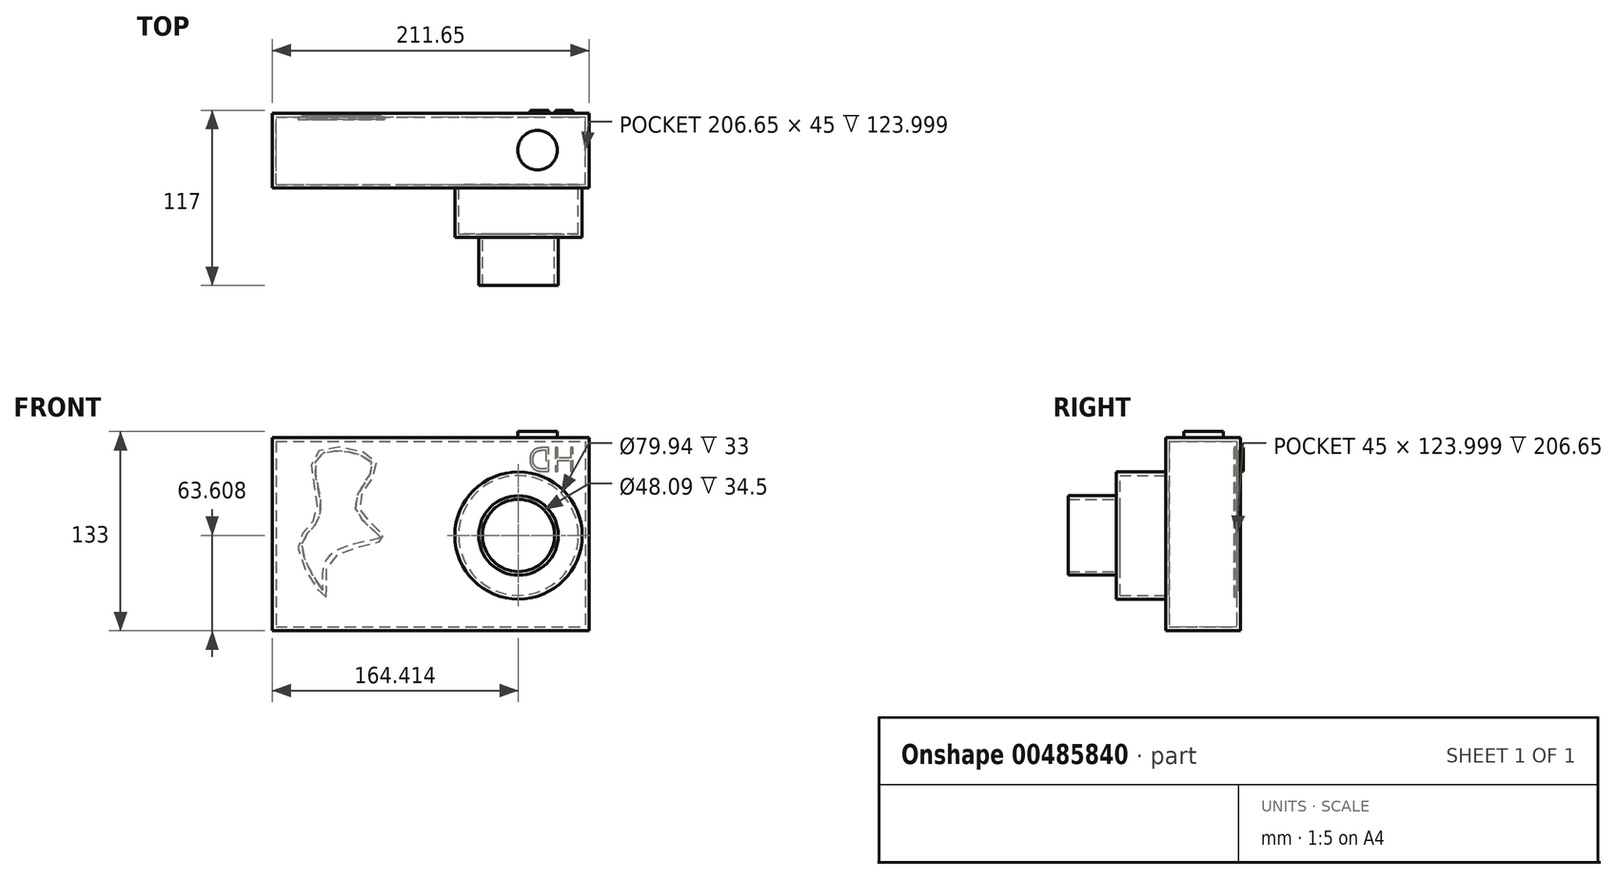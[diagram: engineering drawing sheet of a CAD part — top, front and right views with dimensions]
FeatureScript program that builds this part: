
annotation { "Feature Type Name" : "Feature", "Feature Type Description" : "" }
export const myFeature = defineFeature(function(context is Context, id is Id, definition is map)
    precondition{}
    {
        {
            var Q0;
            Q0=qCreatedBy(makeId("Front.planeOp"),FACE);
            var sketch = newSketch(context, id + "F0", { "sketchPlane" : qUnion([Q0])});
            skLineSegment(sketch, "E0.bottom", {"start": v(-118.11, 60.74) * mm, "end": v(93.54, 60.74) * mm});
            skLineSegment(sketch, "E0.top", {"start": v(-118.11, -68.26) * mm, "end": v(93.54, -68.26) * mm});
            skLineSegment(sketch, "E0.left", {"start": v(-118.11, 60.74) * mm, "end": v(-118.11, -68.26) * mm});
            skLineSegment(sketch, "E0.right", {"start": v(93.54, 60.74) * mm, "end": v(93.54, -68.26) * mm});
            skSolve(sketch);
        }
        {
            var Q0;
            Q0 = qSketchRegion(id + "F0", true);
            extrude(context, id + "F1", {"entities" : qUnion([Q0]), "depth" : 50 * mm});
        }
        {
            var Q0;
            Q0=makeQuery(id+"F1.opExtrude","CAP_FACE",FACE,{"disambiguationData":[OSD([sQuery(id+"F0.wireOp",EDGE,"E0.bottom"),sQuery(id+"F0.wireOp",EDGE,"E0.top"),sQuery(id+"F0.wireOp",EDGE,"E0.left"),sQuery(id+"F0.wireOp",EDGE,"E0.right")])],"isStart":false});
            var sketch = newSketch(context, id + "F2", { "sketchPlane" : qUnion([Q0])});
            skCircle(sketch, "E1", {"center": v(46.3, -4.65) * mm, "radius": 42.47 * mm});
            skSolve(sketch);
        }
        {
            var Q0;
            Q0 = qSketchRegion(id + "F2", true);
            extrude(context, id + "F3", {"entities" : qUnion([Q0]), "operationType" : NewBodyOperationType.ADD, "depth" : 33 * mm});
        }
        {
            var Q0;
            Q0=makeQuery(id+"F3.opExtrude","CAP_FACE",FACE,{"disambiguationData":[OSD([sQuery(id+"F2.wireOp",EDGE,"E1")])],"isStart":false});
            var sketch = newSketch(context, id + "F4", { "sketchPlane" : qUnion([Q0])});
            skCircle(sketch, "E2", {"center": v(46.3, -4.65) * mm, "radius": 26.55 * mm});
            skSolve(sketch);
        }
        {
            var Q0;
            Q0 = qSketchRegion(id + "F4", true);
            extrude(context, id + "F5", {"entities" : qUnion([Q0]), "operationType" : NewBodyOperationType.ADD, "depth" : 32 * mm});
        }
        {
            var Q0;
            Q0=makeQuery(id+"F5.opExtrude","CAP_FACE",FACE,{"disambiguationData":[OSD([sQuery(id+"F4.wireOp",EDGE,"E2")])],"isStart":false});
            shell(context, id + "F6", {"entities" : qUnion([Q0]), "thickness" : 2.5 * mm});
        }
        {
            var Q0;
            Q0=makeQuery(id+"F1.opExtrude","SWEPT_FACE",FACE,{"disambiguationData":[OSD([sQuery(id+"F0.wireOp",EDGE,"E0.bottom")])]});
            var sketch = newSketch(context, id + "F7", { "sketchPlane" : qUnion([Q0])});
            skCircle(sketch, "E3", {"center": v(58.96, -24.66) * mm, "radius": 13.16 * mm});
            skSolve(sketch);
        }
        {
            var Q0;
            Q0 = qSketchRegion(id + "F7", true);
            extrude(context, id + "F8", {"entities" : qUnion([Q0]), "operationType" : NewBodyOperationType.ADD, "depth" : 3 * mm});
        }
        {
            var Q0;
            Q0=makeQuery(id+"F1.opExtrude","CAP_FACE",FACE,{"disambiguationData":[OSD([sQuery(id+"F0.wireOp",EDGE,"E0.bottom"),sQuery(id+"F0.wireOp",EDGE,"E0.top"),sQuery(id+"F0.wireOp",EDGE,"E0.left"),sQuery(id+"F0.wireOp",EDGE,"E0.right")])],"isStart":true});
            var sketch = newSketch(context, id + "F9", { "sketchPlane" : qUnion([Q0])});
            skText(sketch, "E4", { "text": "HD\n", "fontName": "OpenSans-Regular.ttf"});
            const initialGuessF9  = {"E4": [-0.08494, 0.03816, 1, 0, 0.01586]};
            skSetInitialGuess(sketch, initialGuessF9);
            skSolve(sketch);
        }
        {
            var Q0;
            Q0 = qSketchRegion(id + "F9", true);
            extrude(context, id + "F10", {"entities" : qUnion([Q0]), "operationType" : NewBodyOperationType.ADD, "depth" : 2 * mm});
        }
        {
            var Q0;
            {var subQ0=sQuery(id+"F0.wireOp",EDGE,"E0.left");var subQ1=sQuery(id+"F0.wireOp",EDGE,"E0.top");var subQ2=sQuery(id+"F0.wireOp",EDGE,"E0.right");var subQ3=sQuery(id+"F0.wireOp",EDGE,"E0.bottom");Q0=makeQuery(id+"F10.boolean.opBoolean","SPLIT",FACE,{"disambiguationData":[TD([makeQuery(id+"F1.opExtrude","SWEPT_FACE",FACE,{"disambiguationData":[OSD([subQ3])]})])],"derivedFrom":makeQuery(id+"F1.opExtrude","CAP_FACE",FACE,{"disambiguationData":[OSD([subQ3,subQ1,subQ0,subQ2])],"isStart":true})});}
            var sketch = newSketch(context, id + "F11", { "sketchPlane" : qUnion([Q0])});
            skFitSpline(sketch, "E5", {"points": [v(82.06, -45.9) * mm, v(79.37, -21.6) * mm, v(43.07, -6.52) * mm, v(60.04, 14.72) * mm, v(48.56, 43.93) * mm, v(88.85, 50.34) * mm, v(88.38, 10.21) * mm, v(100.83, -11.42) * mm, v(82.06, -45.9) * mm]});
            skSolve(sketch);
        }
        {
            var Q0;
            Q0=makeQuery(id+"F11.imprint","IMPRINT",FACE,{"disambiguationData":[TD([[makeQuery(id+"F11.imprint","IMPRINT",EDGE,{"derivedFrom":sQuery(id+"F11.wireOp",EDGE,"E5")}),-1.0]])]});
            extrude(context, id + "F12", {"entities" : qUnion([Q0]), "operationType" : NewBodyOperationType.ADD, "oppositeDirection" : true, "depth" : 4 * mm});
        }
        {
            var Q0;
            {var subQ0=sQuery(id+"F0.wireOp",EDGE,"E0.left");var subQ1=sQuery(id+"F0.wireOp",EDGE,"E0.top");var subQ2=sQuery(id+"F0.wireOp",EDGE,"E0.right");var subQ3=sQuery(id+"F0.wireOp",EDGE,"E0.bottom");Q0=makeQuery(id+"F10.boolean.opBoolean","SPLIT",FACE,{"disambiguationData":[TD([makeQuery(id+"F1.opExtrude","SWEPT_FACE",FACE,{"disambiguationData":[OSD([subQ3])]})])],"derivedFrom":makeQuery(id+"F1.opExtrude","CAP_FACE",FACE,{"disambiguationData":[OSD([subQ3,subQ1,subQ0,subQ2])],"isStart":true})});}
            var Q1;
            Q1=makeQuery(id+"FQS3LPZwv6cw0UI_1.opFillet","BLEND_FACE",FACE,{"disambiguationData":[OSD([sQuery(id+"F7.wireOp",EDGE,"E3")])]});
            shell(context, id + "F13", {"entities" : qUnion([Q0, Q1]), "thickness" : 2.5 * mm});
        }
        {
            var Q0;
            Q0=makeQuery(id+"F8.opExtrude","CAP_FACE",FACE,{"disambiguationData":[OSD([sQuery(id+"F7.wireOp",EDGE,"E3")])],"isStart":false});
            extrude(context, id + "F14", {"entities" : qUnion([Q0]), "operationType" : NewBodyOperationType.ADD, "depth" : 1 * mm});
        }
    });
